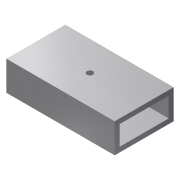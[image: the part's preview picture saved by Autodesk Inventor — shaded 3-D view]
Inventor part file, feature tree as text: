
AUTODESK INVENTOR PART (.ipt)
format: ipt  version: 2014 (Build 180170000, 170)  size: 87,040 bytes
history: native  units: mm
features: extrude x2, sketch x2
ambient origin geometry x8: Origin, YZ Plane, XZ Plane, XY Plane, X Axis, Y Axis, Z Axis, Center Point
bodies: Solid1 (feature_tree)
feature tree (4):
  extrude  "Extrusion1"  Depth=19.05mm
  extrude  "Extrusion2"  Depth=3.175mm
  sketch  "Sketch1"  dims[d0=38.1mm d1=19.05mm]
  sketch  "Sketch2"  dims[d2=3.175mm d3=3.175mm d4=70.0mm d5=0.0mm d6=4.0mm d7=10.0mm d8=0.0mm]
